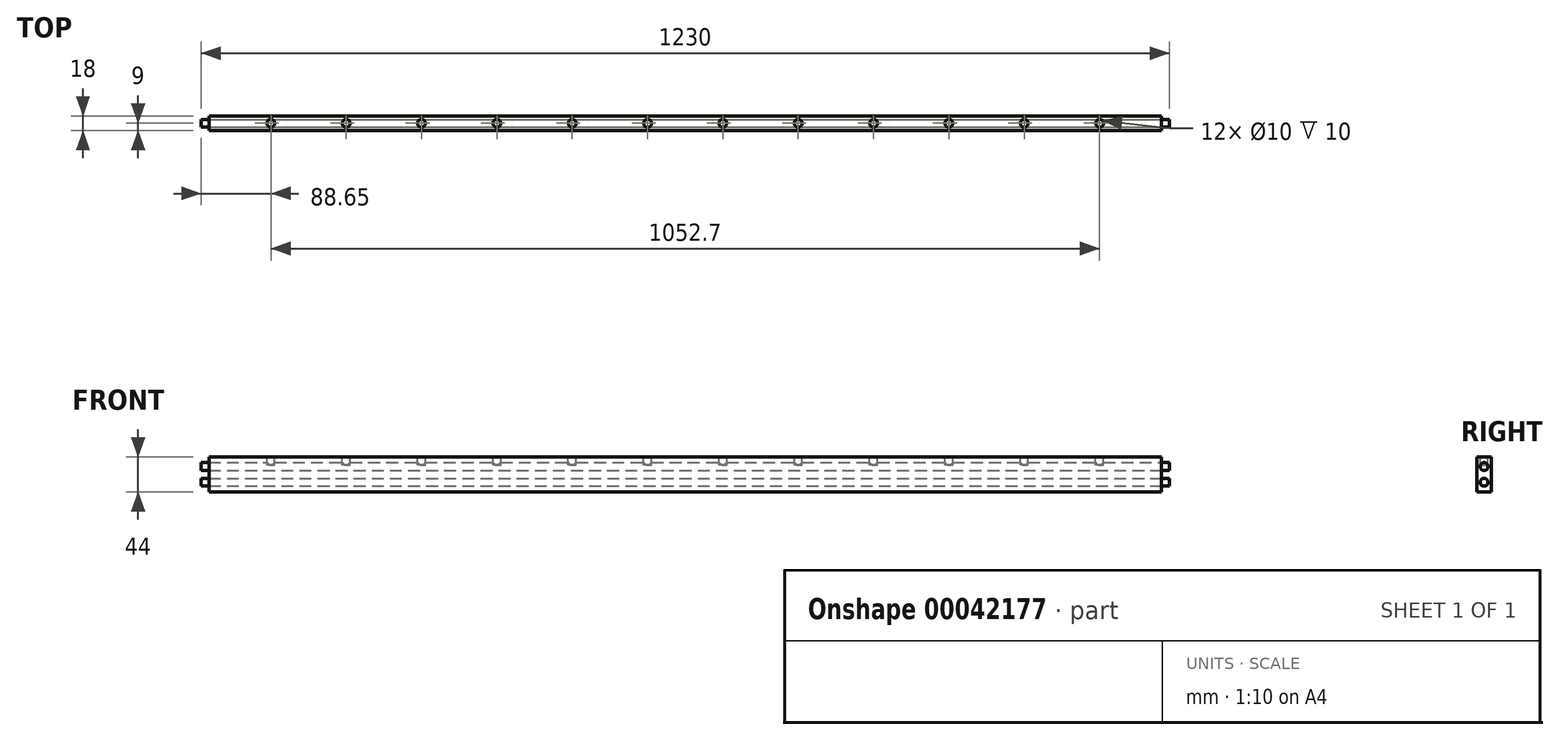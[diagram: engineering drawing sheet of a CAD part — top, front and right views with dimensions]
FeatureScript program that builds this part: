
annotation { "Feature Type Name" : "Feature", "Feature Type Description" : "" }
export const myFeature = defineFeature(function(context is Context, id is Id, definition is map)
    precondition{}
    {
        {
            var Q0;
            Q0=qCreatedBy(makeId("Top.planeOp"),FACE);
            var sketch = newSketch(context, id + "F0", { "sketchPlane" : qUnion([Q0])});
            skLineSegment(sketch, "E0", {"start": v(0, 0) * mm, "end": v(1210, 0) * mm});
            skLineSegment(sketch, "E1", {"start": v(1210, 0) * mm, "end": v(1210, 18) * mm});
            skLineSegment(sketch, "E2", {"start": v(1210, 18) * mm, "end": v(0, 18) * mm});
            skLineSegment(sketch, "E3", {"start": v(0, 18) * mm, "end": v(0, 0) * mm});
            skSolve(sketch);
        }
        {
            var Q0;
            Q0=makeQuery(id+"F0.imprint","IMPRINT",FACE,{"disambiguationData":[TD([[makeQuery(id+"F0.imprint","IMPRINT",EDGE,{"derivedFrom":sQuery(id+"F0.wireOp",EDGE,"E0")}),1.0]])]});
            extrude(context, id + "F1", {"entities" : qUnion([Q0]), "depth" : 44 * mm});
        }
        {
            var Q0;
            Q0=makeQuery(id+"F1.opExtrude","SWEPT_FACE",FACE,{"disambiguationData":[OSD([sQuery(id+"F0.wireOp",EDGE,"E3")])]});
            var sketch = newSketch(context, id + "F2", { "sketchPlane" : qUnion([Q0])});
            skCircle(sketch, "E4", {"center": v(-9, 12) * mm, "radius": 5 * mm});
            skCircle(sketch, "E5.0.1.0", {"center": v(-9, 32) * mm, "radius": 5 * mm});
            skLineSegment(sketch, "E5.direction1", {"start": v(-9, 12) * mm, "end": v(15, 12) * mm, "construction": true});
            skLineSegment(sketch, "E5.direction2", {"start": v(-9, 12) * mm, "end": v(-9, 32) * mm, "construction": true});
            skSolve(sketch);
        }
        {
            var Q0;
            Q0=makeQuery(id+"F2.imprint","IMPRINT",FACE,{"disambiguationData":[TD([[makeQuery(id+"F2.imprint","IMPRINT",EDGE,{"derivedFrom":sQuery(id+"F2.wireOp",EDGE,"E5.0.1.0")}),1.0]])]});
            var Q1;
            Q1=makeQuery(id+"F2.imprint","IMPRINT",FACE,{"disambiguationData":[TD([[makeQuery(id+"F2.imprint","IMPRINT",EDGE,{"derivedFrom":sQuery(id+"F2.wireOp",EDGE,"E4")}),1.0]])]});
            var Q2;
            Q2=sQuery(id+"F2.wireOp",EDGE,"E5.0.1.0");
            extrude(context, id + "F3", {"entities" : qUnion([Q0, Q1]), "surfaceEntities" : qUnion([Q2]), "depth" : 10 * mm, "hasSecondDirection" : true, "secondDirectionOppositeDirection" : true, "secondDirectionDepth" : 1220 * mm});
        }
        {
            var Q0;
            Q0=makeQuery(id+"F1.opExtrude","CAP_FACE",FACE,{"disambiguationData":[OSD([sQuery(id+"F0.wireOp",EDGE,"E0"),sQuery(id+"F0.wireOp",EDGE,"E1"),sQuery(id+"F0.wireOp",EDGE,"E2"),sQuery(id+"F0.wireOp",EDGE,"E3")])],"isStart":false});
            var sketch = newSketch(context, id + "F4", { "sketchPlane" : qUnion([Q0])});
            skLineSegment(sketch, "E6", {"start": v(0, 9) * mm, "end": v(78.65, 9) * mm, "construction": true});
            skCircle(sketch, "E7", {"center": v(78.65, 9) * mm, "radius": 5 * mm});
            skCircle(sketch, "E8.1.0.0", {"center": v(174.35, 9) * mm, "radius": 5 * mm});
            skCircle(sketch, "E8.2.0.0", {"center": v(270.05, 9) * mm, "radius": 5 * mm});
            skCircle(sketch, "E8.3.0.0", {"center": v(365.75, 9) * mm, "radius": 5 * mm});
            skCircle(sketch, "E8.4.0.0", {"center": v(461.45, 9) * mm, "radius": 5 * mm});
            skCircle(sketch, "E8.5.0.0", {"center": v(557.15, 9) * mm, "radius": 5 * mm});
            skCircle(sketch, "E8.6.0.0", {"center": v(652.85, 9) * mm, "radius": 5 * mm});
            skCircle(sketch, "E8.7.0.0", {"center": v(748.55, 9) * mm, "radius": 5 * mm});
            skCircle(sketch, "E8.8.0.0", {"center": v(844.25, 9) * mm, "radius": 5 * mm});
            skCircle(sketch, "E8.9.0.0", {"center": v(939.95, 9) * mm, "radius": 5 * mm});
            skCircle(sketch, "E8.10.0.0", {"center": v(1035.65, 9) * mm, "radius": 5 * mm});
            skCircle(sketch, "E8.11.0.0", {"center": v(1131.35, 9) * mm, "radius": 5 * mm});
            skLineSegment(sketch, "E8.direction1", {"start": v(78.65, 9) * mm, "end": v(174.35, 9) * mm, "construction": true});
            skSolve(sketch);
        }
        {
            var Q0;
            Q0=makeQuery(id+"F4.imprint","IMPRINT",FACE,{"disambiguationData":[TD([[makeQuery(id+"F4.imprint","IMPRINT",EDGE,{"derivedFrom":sQuery(id+"F4.wireOp",EDGE,"E7")}),1.0]])]});
            var Q1;
            Q1=makeQuery(id+"F4.imprint","IMPRINT",FACE,{"disambiguationData":[TD([[makeQuery(id+"F4.imprint","IMPRINT",EDGE,{"derivedFrom":sQuery(id+"F4.wireOp",EDGE,"E8.1.0.0")}),1.0]])]});
            var Q2;
            Q2=makeQuery(id+"F4.imprint","IMPRINT",FACE,{"disambiguationData":[TD([[makeQuery(id+"F4.imprint","IMPRINT",EDGE,{"derivedFrom":sQuery(id+"F4.wireOp",EDGE,"E8.2.0.0")}),1.0]])]});
            var Q3;
            Q3=makeQuery(id+"F4.imprint","IMPRINT",FACE,{"disambiguationData":[TD([[makeQuery(id+"F4.imprint","IMPRINT",EDGE,{"derivedFrom":sQuery(id+"F4.wireOp",EDGE,"E8.3.0.0")}),1.0]])]});
            var Q4;
            Q4=makeQuery(id+"F4.imprint","IMPRINT",FACE,{"disambiguationData":[TD([[makeQuery(id+"F4.imprint","IMPRINT",EDGE,{"derivedFrom":sQuery(id+"F4.wireOp",EDGE,"E8.4.0.0")}),1.0]])]});
            var Q5;
            Q5=makeQuery(id+"F4.imprint","IMPRINT",FACE,{"disambiguationData":[TD([[makeQuery(id+"F4.imprint","IMPRINT",EDGE,{"derivedFrom":sQuery(id+"F4.wireOp",EDGE,"E8.5.0.0")}),1.0]])]});
            var Q6;
            Q6=makeQuery(id+"F4.imprint","IMPRINT",FACE,{"disambiguationData":[TD([[makeQuery(id+"F4.imprint","IMPRINT",EDGE,{"derivedFrom":sQuery(id+"F4.wireOp",EDGE,"E8.6.0.0")}),1.0]])]});
            var Q7;
            Q7=makeQuery(id+"F4.imprint","IMPRINT",FACE,{"disambiguationData":[TD([[makeQuery(id+"F4.imprint","IMPRINT",EDGE,{"derivedFrom":sQuery(id+"F4.wireOp",EDGE,"E8.7.0.0")}),1.0]])]});
            var Q8;
            Q8=makeQuery(id+"F4.imprint","IMPRINT",FACE,{"disambiguationData":[TD([[makeQuery(id+"F4.imprint","IMPRINT",EDGE,{"derivedFrom":sQuery(id+"F4.wireOp",EDGE,"E8.8.0.0")}),1.0]])]});
            var Q9;
            Q9=makeQuery(id+"F4.imprint","IMPRINT",FACE,{"disambiguationData":[TD([[makeQuery(id+"F4.imprint","IMPRINT",EDGE,{"derivedFrom":sQuery(id+"F4.wireOp",EDGE,"E8.9.0.0")}),1.0]])]});
            var Q10;
            Q10=makeQuery(id+"F4.imprint","IMPRINT",FACE,{"disambiguationData":[TD([[makeQuery(id+"F4.imprint","IMPRINT",EDGE,{"derivedFrom":sQuery(id+"F4.wireOp",EDGE,"E8.10.0.0")}),1.0]])]});
            var Q11;
            Q11=makeQuery(id+"F4.imprint","IMPRINT",FACE,{"disambiguationData":[TD([[makeQuery(id+"F4.imprint","IMPRINT",EDGE,{"derivedFrom":sQuery(id+"F4.wireOp",EDGE,"E8.11.0.0")}),1.0]])]});
            var Q12;
            Q12=makeQuery(id+"F4.imprint","IMPRINT",FACE,{"disambiguationData":[TD([[makeQuery(id+"F4.imprint","IMPRINT",EDGE,{"derivedFrom":sQuery(id+"F4.wireOp",EDGE,"E8.12.0.0")}),1.0]])]});
            var Q13;
            Q13=makeQuery(id+"F4.imprint","IMPRINT",FACE,{"disambiguationData":[TD([[makeQuery(id+"F4.imprint","IMPRINT",EDGE,{"derivedFrom":sQuery(id+"F4.wireOp",EDGE,"E8.13.0.0")}),1.0]])]});
            var Q14;
            Q14=makeQuery(id+"F4.imprint","IMPRINT",FACE,{"disambiguationData":[TD([[makeQuery(id+"F4.imprint","IMPRINT",EDGE,{"derivedFrom":sQuery(id+"F4.wireOp",EDGE,"E8.14.0.0")}),1.0]])]});
            var Q15;
            Q15=makeQuery(id+"F4.imprint","IMPRINT",FACE,{"disambiguationData":[TD([[makeQuery(id+"F4.imprint","IMPRINT",EDGE,{"derivedFrom":sQuery(id+"F4.wireOp",EDGE,"E8.15.0.0")}),1.0]])]});
            extrude(context, id + "F5", {"entities" : qUnion([Q0, Q1, Q2, Q3, Q4, Q5, Q6, Q7, Q8, Q9, Q10, Q11, Q12, Q13, Q14, Q15]), "operationType" : NewBodyOperationType.REMOVE, "oppositeDirection" : true, "depth" : 10 * mm});
        }
    });
